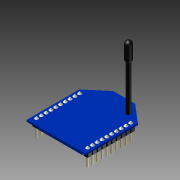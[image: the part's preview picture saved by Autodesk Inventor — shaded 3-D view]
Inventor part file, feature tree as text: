
AUTODESK INVENTOR PART (.ipt)
format: ipt  version: 2012 (Build 160160000, 160)  size: 665,600 bytes
history: native  units: in
note: dims shown in document units (in); Inventor stores cm internally (conversion verified against a paired STEP export)
features: extrude x3, sketch x3, other x2, imported_body x1
ambient origin geometry x8: Origin, YZ Plane, XZ Plane, XY Plane, X Axis, Y Axis, Z Axis, Center Point
feature tree (9):
  other  "XBee"
  other  "XBee1"
  extrude  "Extrusion1"  Depth=0.1575in TaperAngle=0.0deg
  extrude  "Extrusion2"  [1 undecoded]
  extrude  "Extrusion3"  [1 undecoded]
  imported_body  "Base1"
  sketch  "Sketch1"  dims[d0=0.1575in d1=0.0in d2=0.1575in d3=0.0in]
  sketch  "Sketch2"  dims[d4=0.1575in d5=0.0in]
  sketch  "Sketch3"
note: 2 required parameter values undecoded (feature->parameter linkage not recoverable at this tier; creation-order binding heuristic only, values carry confidence <= 0.55)
